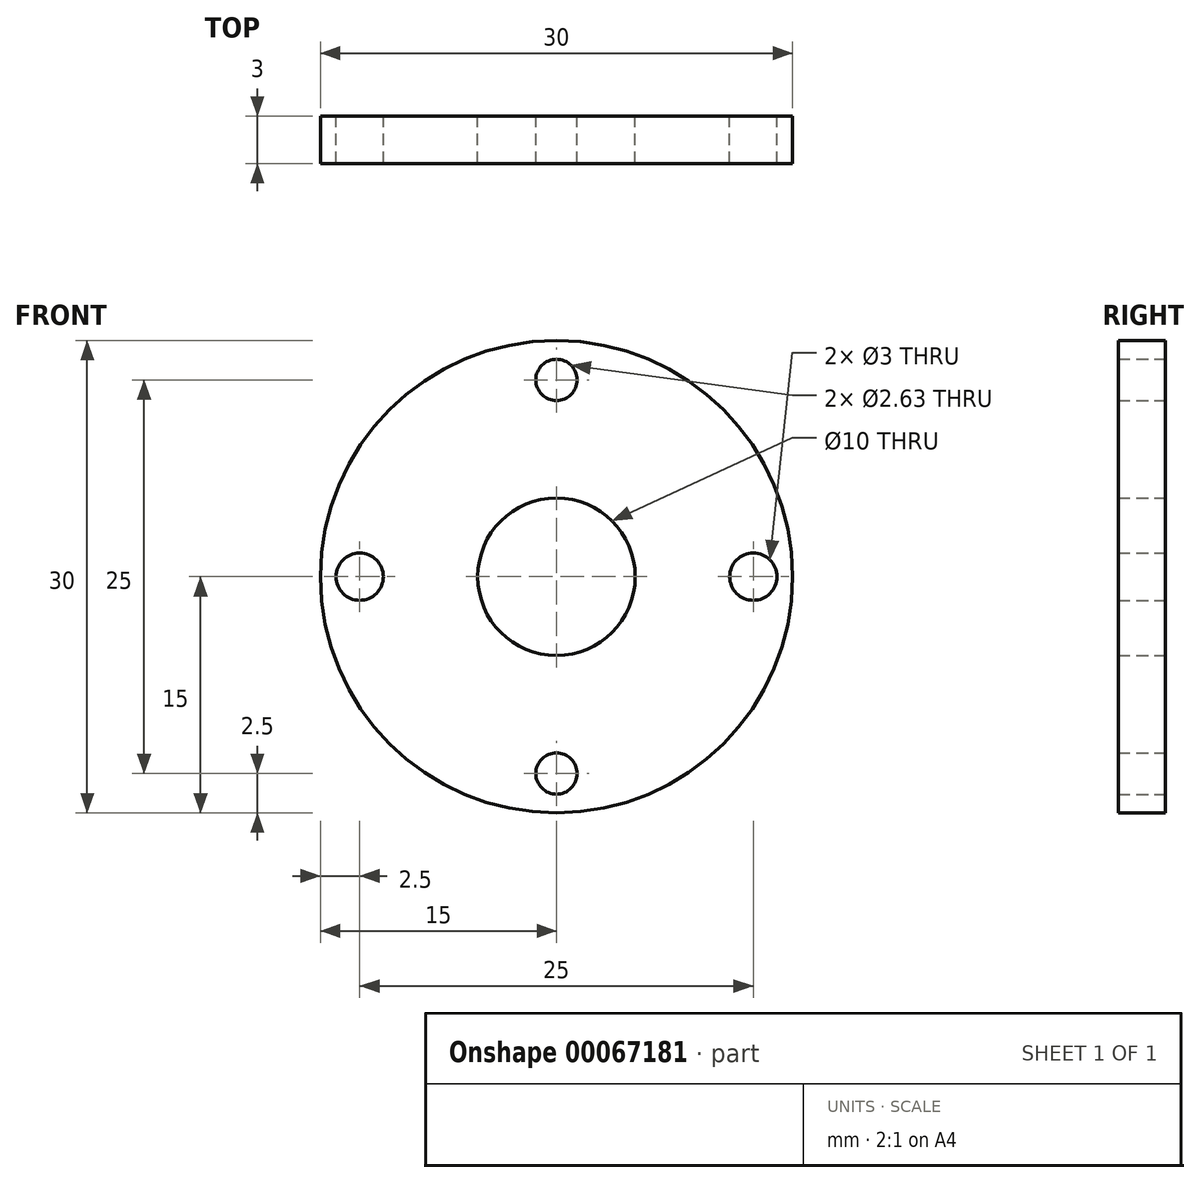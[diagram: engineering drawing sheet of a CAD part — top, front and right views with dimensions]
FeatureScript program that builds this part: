
annotation { "Feature Type Name" : "Feature", "Feature Type Description" : "" }
export const myFeature = defineFeature(function(context is Context, id is Id, definition is map)
    precondition{}
    {
        {
            var Q0;
            Q0=qCreatedBy(makeId("Front.planeOp"),FACE);
            var sketch = newSketch(context, id + "F0", { "sketchPlane" : qUnion([Q0])});
            skCircle(sketch, "E0", {"center": v(0, 0) * mm, "radius": 15 * mm});
            skCircle(sketch, "E1", {"center": v(0, 0) * mm, "radius": 5 * mm});
            skLineSegment(sketch, "E2", {"start": v(0, 19.21) * mm, "end": v(0, -19.7) * mm, "construction": true});
            skLineSegment(sketch, "E3", {"start": v(-21.17, 0) * mm, "end": v(27.6, 0) * mm, "construction": true});
            skCircle(sketch, "E4", {"center": v(-12.5, 0) * mm, "radius": 1.5 * mm});
            skCircle(sketch, "E5", {"center": v(0, 12.5) * mm, "radius": 1.31 * mm});
            skCircle(sketch, "E6.MirrorC", {"center": v(0, -12.5) * mm, "radius": 1.31 * mm});
            skCircle(sketch, "E7.MirrorC", {"center": v(12.5, 0) * mm, "radius": 1.5 * mm});
            skSolve(sketch);
        }
        {
            var Q0;
            Q0=makeQuery(id+"F0.imprint","IMPRINT",FACE,{"disambiguationData":[TD([[makeQuery(id+"F0.imprint","IMPRINT",EDGE,{"derivedFrom":sQuery(id+"F0.wireOp",EDGE,"E0")}),1.0]])]});
            extrude(context, id + "F1", {"entities" : qUnion([Q0]), "depth" : 3 * mm});
        }
    });
